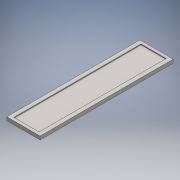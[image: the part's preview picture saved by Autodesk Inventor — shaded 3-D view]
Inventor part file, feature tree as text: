
AUTODESK INVENTOR PART (.ipt)
format: ipt  version: 2016 SP1 (Build 200210100, 210)  size: 101,376 bytes
history: native  units: mm
features: extrude x2, sketch x2
ambient origin geometry x8: Origin, YZ Plane, XZ Plane, XY Plane, X Axis, Y Axis, Z Axis, Center Point
bodies: Solid1 (feature_tree)
feature tree (4):
  extrude  "Extrusion1"  Depth=300.0mm
  extrude  "Extrusion2"  Depth=2.0mm
  sketch  "Sketch1"  dims[d0=75.0mm d1=300.0mm]
  sketch  "Sketch2"  dims[d2=150.0mm d3=37.5mm d4=8.0mm d5=0.0mm d6=57.0mm d7=287.0mm d8=143.5mm d9=28.5mm d10=2.0mm d11=0.0mm]
